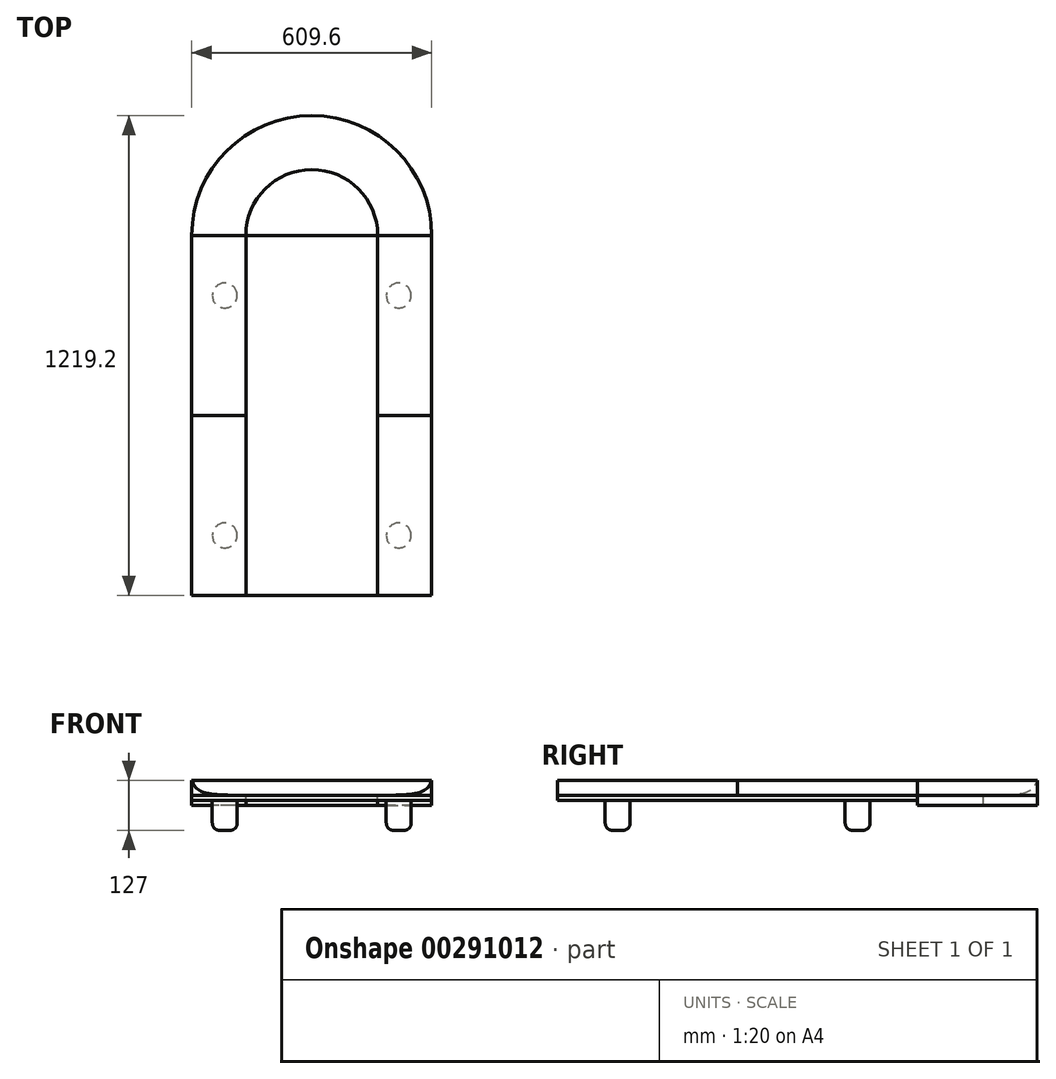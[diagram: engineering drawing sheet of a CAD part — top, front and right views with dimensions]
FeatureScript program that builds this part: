
annotation { "Feature Type Name" : "Feature", "Feature Type Description" : "" }
export const myFeature = defineFeature(function(context is Context, id is Id, definition is map)
    precondition{}
    {
        {
            var Q0;
            Q0=qCreatedBy(makeId("Front.planeOp"),FACE);
            var sketch = newSketch(context, id + "F0", { "sketchPlane" : qUnion([Q0])});
            skLineSegment(sketch, "E0", {"start": v(0, 0) * mm, "end": v(31.75, 0) * mm});
            skLineSegment(sketch, "E1", {"start": v(31.75, 0) * mm, "end": v(31.75, -57.79) * mm});
            skLineSegment(sketch, "E2", {"start": v(13.34, -76.2) * mm, "end": v(0, -76.2) * mm});
            skLineSegment(sketch, "E3", {"start": v(0, -76.2) * mm, "end": v(0, 0) * mm});
            skPoint(sketch, "E4.visualSharp", {"position": v(31.75, -76.2) * mm});
            skArc(sketch, "E4.filletArc", {"start": v(13.34, -76.2) * mm, "mid": v(26.36, -70.8) * mm, "end": v(31.75, -57.79) * mm});
            skSolve(sketch);
        }
        {
            var Q0;
            Q0 = qSketchRegion(id + "F0", true);
            var Q1;
            Q1=sQuery(id+"F0.wireOp",EDGE,"E3");
            revolve(context, id + "F1", {"entities" : qUnion([Q0]), "axis" : qUnion([Q1]), "revolveType" : RevolveType.FULL});
        }
        {
            var Q0;
            Q0=makeQuery(id+"F1.opRevolve","SWEPT_BODY",BODY,{"disambiguationData":[OSD([sQuery(id+"F0.wireOp",EDGE,"E0"),sQuery(id+"F0.wireOp",EDGE,"E1"),sQuery(id+"F0.wireOp",EDGE,"E2"),sQuery(id+"F0.wireOp",EDGE,"E3"),sQuery(id+"F0.wireOp",EDGE,"E4.filletArc")])]});
            transform(context, id + "F2", {"entities" : qUnion([Q0]), "transformType" : TransformType.TRANSLATION_3D, "dx" : 220.98 * mm, "dy" : 304.8 * mm, "dz" : 0 * mm, "makeCopy" : false});
        }
        {
            var Q0;
            Q0=makeQuery(id+"F1.opRevolve","SWEPT_BODY",BODY,{"disambiguationData":[OSD([sQuery(id+"F0.wireOp",EDGE,"E0"),sQuery(id+"F0.wireOp",EDGE,"E1"),sQuery(id+"F0.wireOp",EDGE,"E2"),sQuery(id+"F0.wireOp",EDGE,"E3"),sQuery(id+"F0.wireOp",EDGE,"E4.filletArc")])]});
            var Q1;
            Q1=qCreatedBy(makeId("Front.planeOp"),FACE);
            mirror(context, id + "F3", {"entities" : qUnion([Q0]), "mirrorPlane" : qUnion([Q1])});
        }
        {
            var Q0;
            Q0=makeQuery(id+"F1.opRevolve","SWEPT_BODY",BODY,{"disambiguationData":[OSD([sQuery(id+"F0.wireOp",EDGE,"E0"),sQuery(id+"F0.wireOp",EDGE,"E1"),sQuery(id+"F0.wireOp",EDGE,"E2"),sQuery(id+"F0.wireOp",EDGE,"E3"),sQuery(id+"F0.wireOp",EDGE,"E4.filletArc")])]});
            var Q1;
            Q1=makeQuery(id+"F3.opPattern","COPY",BODY,{"derivedFrom":makeQuery(id+"F1.opRevolve","SWEPT_BODY",BODY,{"disambiguationData":[OSD([sQuery(id+"F0.wireOp",EDGE,"E0"),sQuery(id+"F0.wireOp",EDGE,"E1"),sQuery(id+"F0.wireOp",EDGE,"E2"),sQuery(id+"F0.wireOp",EDGE,"E3"),sQuery(id+"F0.wireOp",EDGE,"E4.filletArc")])]}),"instanceName":"1"});
            var Q2;
            Q2=qCreatedBy(makeId("Right.planeOp"),FACE);
            mirror(context, id + "F4", {"entities" : qUnion([Q0, Q1]), "mirrorPlane" : qUnion([Q2])});
        }
        {
            var Q0;
            Q0=qCreatedBy(makeId("Top.planeOp"),FACE);
            var sketch = newSketch(context, id + "F5", { "sketchPlane" : qUnion([Q0])});
            skLineSegment(sketch, "E5", {"start": v(0, 0) * mm, "end": v(0, 457.2) * mm, "construction": true});
            skLineSegment(sketch, "E6", {"start": v(0, 0) * mm, "end": v(0, -457.2) * mm, "construction": true});
            skLineSegment(sketch, "E7", {"start": v(0, 0) * mm, "end": v(304.8, 0) * mm, "construction": true});
            skLineSegment(sketch, "E8", {"start": v(0, 0) * mm, "end": v(-304.8, 0) * mm, "construction": true});
            skLineSegment(sketch, "E9", {"start": v(0, 457.2) * mm, "end": v(304.8, 457.2) * mm});
            skLineSegment(sketch, "E10", {"start": v(304.8, 457.2) * mm, "end": v(304.8, 0) * mm});
            skLineSegment(sketch, "E11", {"start": v(304.8, 0) * mm, "end": v(304.8, -457.2) * mm});
            skLineSegment(sketch, "E12", {"start": v(304.8, -457.2) * mm, "end": v(0, -457.2) * mm});
            skLineSegment(sketch, "E13", {"start": v(0, -457.2) * mm, "end": v(-304.8, -457.2) * mm});
            skLineSegment(sketch, "E14", {"start": v(-304.8, -457.2) * mm, "end": v(-304.8, 0) * mm});
            skLineSegment(sketch, "E15", {"start": v(-304.8, 0) * mm, "end": v(-304.8, 457.2) * mm});
            skLineSegment(sketch, "E16", {"start": v(-304.8, 457.2) * mm, "end": v(0, 457.2) * mm});
            skSolve(sketch);
        }
        {
            var Q0;
            Q0=qCreatedBy(makeId("Front.planeOp"),FACE);
            var sketch = newSketch(context, id + "F6", { "sketchPlane" : qUnion([Q0])});
            skLineSegment(sketch, "E17.0", {"start": v(0, 0) * mm, "end": v(304.8, 0) * mm, "construction": true});
            skFitSpline(sketch, "E18", {"points": [v(304.8, 38.1) * mm, v(286.25, 12.77) * mm, v(167.56, 0) * mm], "startDerivative": vector(-33.45, -82.63) * mm, "endDerivative": vector(-218.82, -1.06) * mm});
            skLineSegment(sketch, "E19", {"start": v(304.8, 38.1) * mm, "end": v(304.8, 0) * mm});
            skLineSegment(sketch, "E20", {"start": v(167.56, 0) * mm, "end": v(304.8, 0) * mm});
            skSolve(sketch);
        }
        {
            var Q0;
            Q0=makeQuery(id+"F6.imprint","IMPRINT",FACE,{"disambiguationData":[TD([[makeQuery(id+"F6.imprint","IMPRINT",EDGE,{"derivedFrom":sQuery(id+"F6.wireOp",EDGE,"E18")}),1.0]])]});
            var Q1;
            Q1=sQuery(id+"F6.wireOp",EDGE,"E18");
            var Q2;
            Q2=sQuery(id+"F6.wireOp",EDGE,"E19");
            var Q3;
            Q3=sQuery(id+"F6.wireOp",EDGE,"E20");
            extrude(context, id + "F7", {"entities" : qUnion([Q0]), "surfaceEntities" : qUnion([Q1, Q2, Q3]), "depth" : 457.2 * mm});
        }
        {
            var Q0;
            Q0=makeQuery(id+"F7.opExtrude","SWEPT_BODY",BODY,{"disambiguationData":[OSD([sQuery(id+"F6.wireOp",EDGE,"E18")])]});
            var Q1;
            Q1=qCreatedBy(makeId("Front.planeOp"),FACE);
            mirror(context, id + "F8", {"entities" : qUnion([Q0]), "mirrorPlane" : qUnion([Q1])});
        }
        {
            var Q0;
            Q0=makeQuery(id+"F8.opPattern","COPY",BODY,{"derivedFrom":makeQuery(id+"F7.opExtrude","SWEPT_BODY",BODY,{"disambiguationData":[OSD([sQuery(id+"F6.wireOp",EDGE,"E18")])]}),"instanceName":"1"});
            var Q1;
            Q1=makeQuery(id+"F7.opExtrude","SWEPT_BODY",BODY,{"disambiguationData":[OSD([sQuery(id+"F6.wireOp",EDGE,"E18")])]});
            var Q2;
            Q2=qCreatedBy(makeId("Right.planeOp"),FACE);
            mirror(context, id + "F9", {"entities" : qUnion([Q0, Q1]), "mirrorPlane" : qUnion([Q2])});
        }
        {
            var Q0;
            Q0 = qSketchRegion(id + "F5", true);
            extrude(context, id + "F10", {"entities" : qUnion([Q0]), "depth" : 12.7 * mm});
        }
        {
            var Q0;
            Q0=makeQuery(id+"F7.opExtrude","SWEPT_BODY",BODY,{"disambiguationData":[OSD([sQuery(id+"F6.wireOp",EDGE,"E18")])]});
            var Q1;
            Q1=makeQuery(id+"F8.opPattern","COPY",BODY,{"derivedFrom":makeQuery(id+"F7.opExtrude","SWEPT_BODY",BODY,{"disambiguationData":[OSD([sQuery(id+"F6.wireOp",EDGE,"E18")])]}),"instanceName":"1"});
            var Q2;
            Q2=makeQuery(id+"F9.opPattern","COPY",BODY,{"derivedFrom":makeQuery(id+"F7.opExtrude","SWEPT_BODY",BODY,{"disambiguationData":[OSD([sQuery(id+"F6.wireOp",EDGE,"E18")])]}),"instanceName":"1"});
            var Q3;
            Q3=makeQuery(id+"F9.opPattern","COPY",BODY,{"derivedFrom":makeQuery(id+"F8.opPattern","COPY",BODY,{"derivedFrom":makeQuery(id+"F7.opExtrude","SWEPT_BODY",BODY,{"disambiguationData":[OSD([sQuery(id+"F6.wireOp",EDGE,"E18")])]}),"instanceName":"1"}),"instanceName":"1"});
            transform(context, id + "F11", {"entities" : qUnion([Q0, Q1, Q2, Q3]), "transformType" : TransformType.TRANSLATION_3D, "dx" : 0 * mm, "dy" : 0 * mm, "dz" : 12.7 * mm, "makeCopy" : false});
        }
        {
            var Q0;
            Q0=makeQuery(id+"F10.opExtrude","CAP_FACE",FACE,{"disambiguationData":[OSD([sQuery(id+"F5.wireOp",EDGE,"E9"),sQuery(id+"F5.wireOp",EDGE,"E10"),sQuery(id+"F5.wireOp",EDGE,"E11"),sQuery(id+"F5.wireOp",EDGE,"E12"),sQuery(id+"F5.wireOp",EDGE,"E13"),sQuery(id+"F5.wireOp",EDGE,"E14"),sQuery(id+"F5.wireOp",EDGE,"E15"),sQuery(id+"F5.wireOp",EDGE,"E16")])],"isStart":false});
            var sketch = newSketch(context, id + "F12", { "sketchPlane" : qUnion([Q0])});
            skLineSegment(sketch, "E21.0", {"start": v(167.56, 457.2) * mm, "end": v(167.56, 0) * mm});
            skLineSegment(sketch, "E22.0", {"start": v(-167.56, 457.2) * mm, "end": v(-167.56, 0) * mm});
            skArc(sketch, "E23", {"start": v(167.56, 457.2) * mm, "mid": v(0, 624.76) * mm, "end": v(-167.56, 457.2) * mm});
            skLineSegment(sketch, "E24.0", {"start": v(304.8, 457.2) * mm, "end": v(304.8, 0) * mm});
            skLineSegment(sketch, "E25.0", {"start": v(-304.8, -457.2) * mm, "end": v(-304.8, 457.2) * mm});
            skArc(sketch, "E26", {"start": v(304.8, 457.2) * mm, "mid": v(0, 762) * mm, "end": v(-304.8, 457.2) * mm});
            skSolve(sketch);
        }
        {
            var Q0;
            Q0=makeQuery(id+"F8.opPattern","COPY",FACE,{"derivedFrom":makeQuery(id+"F7.opExtrude","CAP_FACE",FACE,{"disambiguationData":[OSD([sQuery(id+"F6.wireOp",EDGE,"E18"),sQuery(id+"F6.wireOp",EDGE,"E19"),sQuery(id+"F6.wireOp",EDGE,"E20")])],"isStart":false}),"instanceName":"1"});
            var Q1;
            Q1=sQuery(id+"F12.wireOp",EDGE,"E23");
            sweep(context, id + "F13", {"profiles" : qUnion([Q0]), "path" : qUnion([Q1])});
        }
        {
            var Q0;
            Q0=makeQuery(id+"F13.opSweep","SWEPT_FACE",FACE,{"disambiguationData":[OSD([sQuery(id+"F6.wireOp",EDGE,"E20"),sQuery(id+"F12.wireOp",EDGE,"E23")])]});
            extrude(context, id + "F14", {"entities" : qUnion([Q0]), "depth" : 25.4 * mm});
        }
    });
